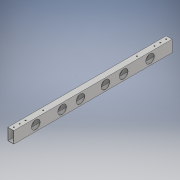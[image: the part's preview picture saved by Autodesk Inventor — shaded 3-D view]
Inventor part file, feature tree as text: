
AUTODESK INVENTOR PART (.ipt)
format: ipt  version: 2018 (Build 220112000, 112)  size: 161,792 bytes
history: native  units: in
note: dims shown in document units (in); Inventor stores cm internally (conversion verified against a paired STEP export)
features: extrude x3, sketch x3
ambient origin geometry x8: Origin, YZ Plane, XZ Plane, XY Plane, X Axis, Y Axis, Z Axis, Center Point
bodies: Solid1 (feature_tree)
feature tree (6):
  extrude  "Extrusion1"  Depth=2.0in
  extrude  "Extrusion2"  Depth=27.0in TaperAngle=0.0deg
  extrude  "Extrusion5"  Depth=1.0in
  sketch  "Sketch1"  dims[d0=1.0in d1=2.0in]
  sketch  "Sketch2"  dims[d2=0.0625in d3=27.0in d4=0.0in]
  sketch  "Sketch3"  dims[d5=3.75in d6=8.25in d7=11.375in d8=1.5in d9=1.5in d10=1.5in d11=27.0in d12=0.0in d13=1.5in d14=1.0in d15=3.0in d16=1.5in d17=1.0in d18=3.0in d19=0.2031in d24=0.5in d25=0.5in d26=8.5in d27=0.0in]
